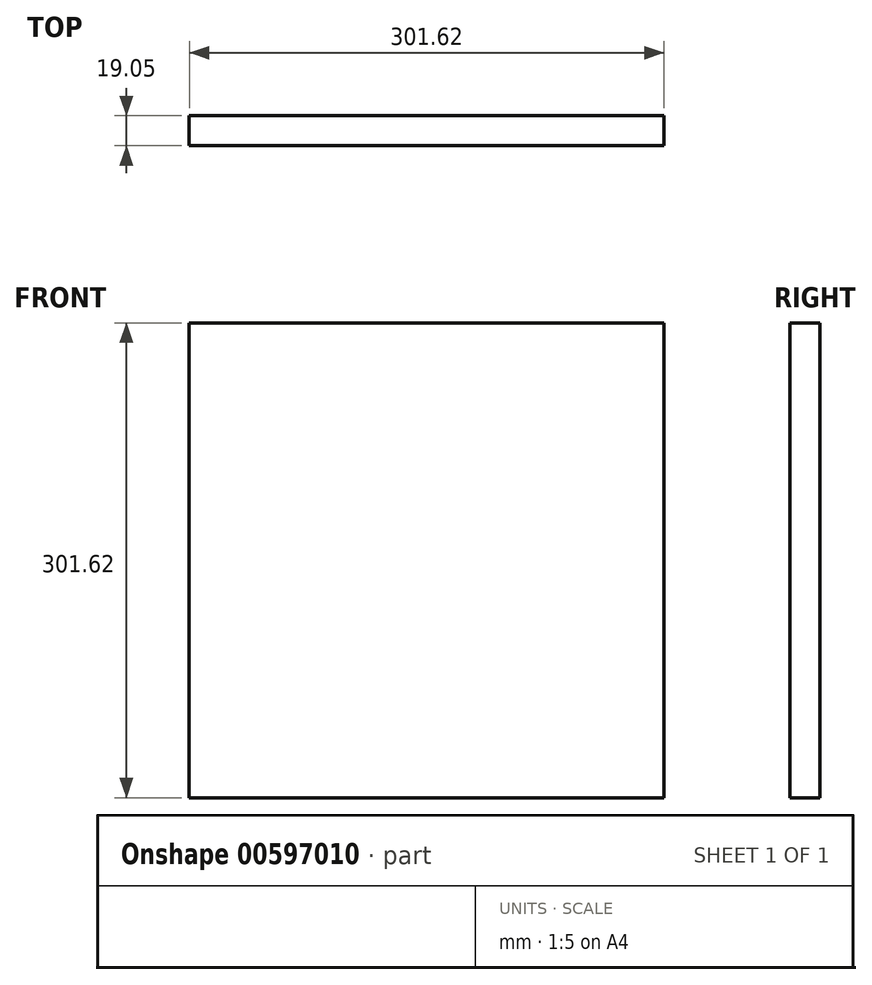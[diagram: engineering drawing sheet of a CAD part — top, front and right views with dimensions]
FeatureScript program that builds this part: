
annotation { "Feature Type Name" : "Feature", "Feature Type Description" : "" }
export const myFeature = defineFeature(function(context is Context, id is Id, definition is map)
    precondition{}
    {
        {
            var Q0;
            Q0=qCreatedBy(makeId("Front.planeOp"),FACE);
            var sketch = newSketch(context, id + "F0", { "sketchPlane" : qUnion([Q0])});
            skLineSegment(sketch, "E0.bottom", {"start": v(-150.81, 150.81) * mm, "end": v(150.81, 150.81) * mm});
            skLineSegment(sketch, "E0.top", {"start": v(-150.81, -150.81) * mm, "end": v(150.81, -150.81) * mm});
            skLineSegment(sketch, "E0.left", {"start": v(-150.81, 150.81) * mm, "end": v(-150.81, -150.81) * mm});
            skLineSegment(sketch, "E0.right", {"start": v(150.81, 150.81) * mm, "end": v(150.81, -150.81) * mm});
            skPoint(sketch, "E0.middle", {"position": v(0, 0) * mm});
            skSolve(sketch);
        }
        {
            var Q0;
            Q0 = qSketchRegion(id + "F0", true);
            extrude(context, id + "F1", {"entities" : qUnion([Q0]), "oppositeDirection" : true, "depth" : 19.05 * mm, "offsetDistance" : 25.4 * mm});
        }
    });
